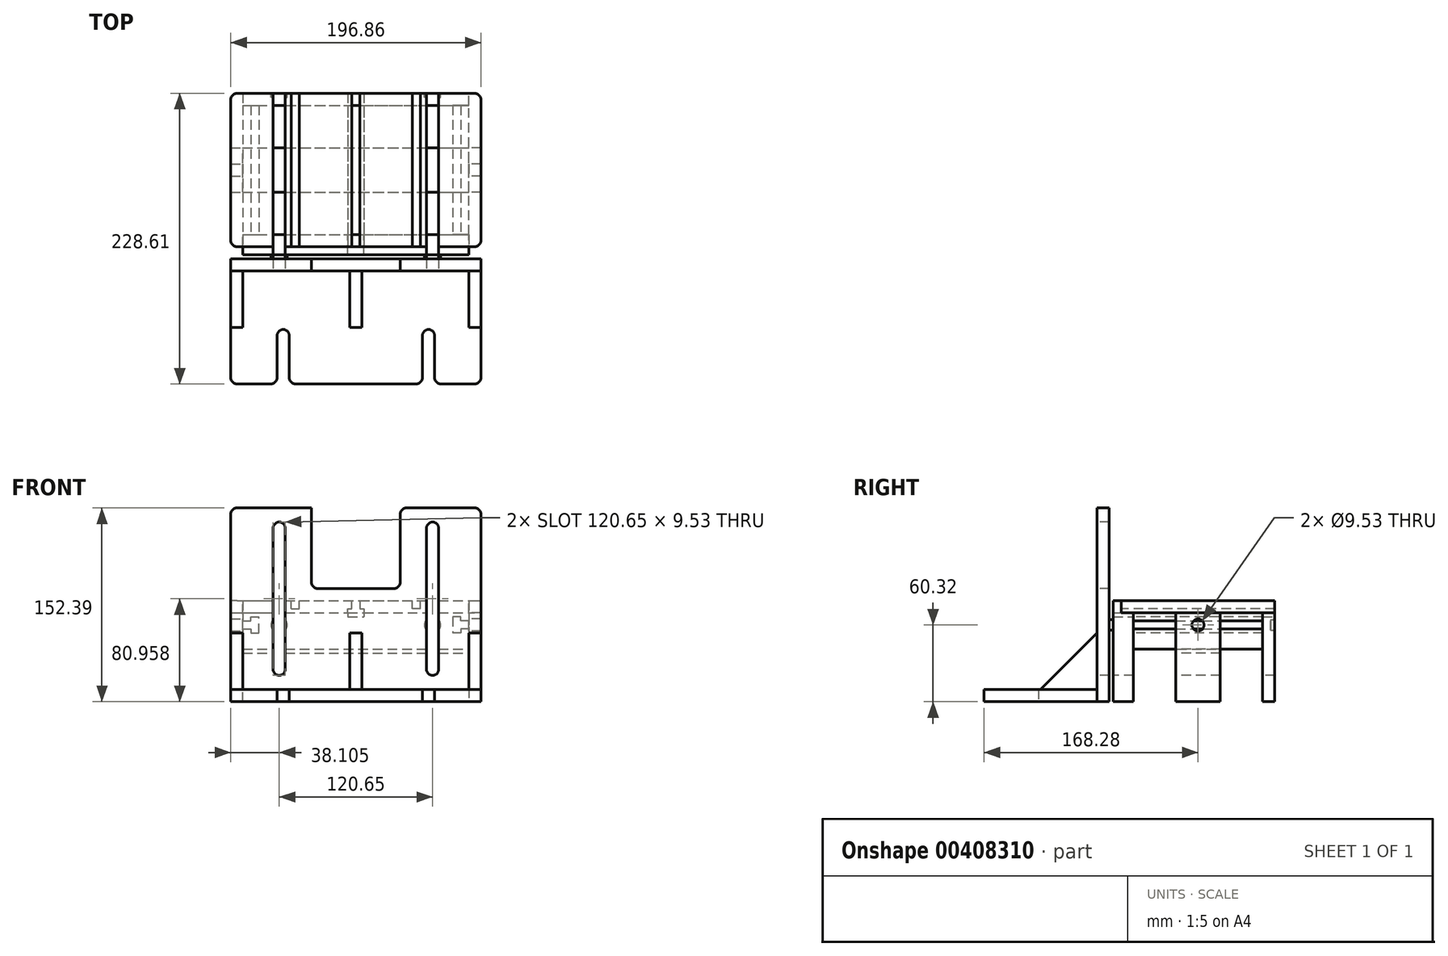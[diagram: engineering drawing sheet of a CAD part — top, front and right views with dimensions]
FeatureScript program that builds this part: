
annotation { "Feature Type Name" : "Feature", "Feature Type Description" : "" }
export const myFeature = defineFeature(function(context is Context, id is Id, definition is map)
    precondition{}
    {
        {
            var Q0;
            Q0=qCreatedBy(makeId("Top.planeOp"),FACE);
            var sketch = newSketch(context, id + "F0", { "sketchPlane" : qUnion([Q0])});
            skLineSegment(sketch, "E0.bottom", {"start": v(-98.42, 60.33) * mm, "end": v(98.43, 60.33) * mm});
            skLineSegment(sketch, "E0.top", {"start": v(-98.43, -60.33) * mm, "end": v(98.42, -60.33) * mm});
            skLineSegment(sketch, "E0.left", {"start": v(-98.42, 60.32) * mm, "end": v(-98.43, -60.33) * mm});
            skLineSegment(sketch, "E0.right", {"start": v(98.43, 60.33) * mm, "end": v(98.42, -60.33) * mm});
            skLineSegment(sketch, "E1", {"start": v(-98.43, 60.33) * mm, "end": v(98.43, -60.33) * mm, "construction": true});
            skSolve(sketch);
        }
        {
            var Q0;
            Q0 = qSketchRegion(id + "F0", true);
            extrude(context, id + "F1", {"entities" : qUnion([Q0]), "depth" : 38.1 * mm});
        }
        {
            var Q0;
            Q0=makeQuery(id+"F1.opExtrude","SWEPT_FACE",FACE,{"disambiguationData":[OSD([sQuery(id+"F0.wireOp",EDGE,"E0.top")])]});
            var sketch = newSketch(context, id + "F2", { "sketchPlane" : qUnion([Q0])});
            skLineSegment(sketch, "E2", {"start": v(-98.43, 19.05) * mm, "end": v(98.43, 19.05) * mm, "construction": true});
            skLineSegment(sketch, "E3", {"start": v(0, 38.1) * mm, "end": v(0, 0) * mm, "construction": true});
            skLineSegment(sketch, "E4", {"start": v(-98.43, 19.05) * mm, "end": v(-98.43, 22.23) * mm});
            skLineSegment(sketch, "E5", {"start": v(-98.42, 22.23) * mm, "end": v(-82.55, 22.23) * mm});
            skLineSegment(sketch, "E6", {"start": v(-82.55, 22.23) * mm, "end": v(-82.55, 25.4) * mm});
            skLineSegment(sketch, "E7", {"start": v(-82.55, 25.4) * mm, "end": v(-76.2, 25.4) * mm});
            skLineSegment(sketch, "E8", {"start": v(-76.2, 25.4) * mm, "end": v(-76.2, 19.05) * mm});
            skLineSegment(sketch, "E9.MirrorCS", {"start": v(-82.55, 15.88) * mm, "end": v(-82.55, 12.7) * mm});
            skLineSegment(sketch, "E10.MirrorCS", {"start": v(-76.2, 12.7) * mm, "end": v(-76.2, 19.05) * mm});
            skLineSegment(sketch, "E11.MirrorCS", {"start": v(-82.55, 12.7) * mm, "end": v(-76.2, 12.7) * mm});
            skLineSegment(sketch, "E12.MirrorCS", {"start": v(-98.42, 15.88) * mm, "end": v(-82.55, 15.88) * mm});
            skLineSegment(sketch, "E13.MirrorCS", {"start": v(-98.43, 19.05) * mm, "end": v(-98.43, 15.88) * mm});
            skLineSegment(sketch, "E14.MirrorCS", {"start": v(82.55, 22.23) * mm, "end": v(82.55, 25.4) * mm});
            skLineSegment(sketch, "E15.MirrorCS", {"start": v(98.42, 19.05) * mm, "end": v(98.42, 15.87) * mm});
            skLineSegment(sketch, "E16.MirrorCS", {"start": v(76.2, 25.4) * mm, "end": v(76.2, 19.05) * mm});
            skLineSegment(sketch, "E17.MirrorCS", {"start": v(82.55, 25.4) * mm, "end": v(76.2, 25.4) * mm});
            skLineSegment(sketch, "E18.MirrorCS", {"start": v(98.42, 22.23) * mm, "end": v(82.55, 22.23) * mm});
            skLineSegment(sketch, "E19.MirrorCS", {"start": v(98.42, 19.05) * mm, "end": v(98.42, 22.23) * mm});
            skLineSegment(sketch, "E20.MirrorCS", {"start": v(82.55, 15.87) * mm, "end": v(82.55, 12.7) * mm});
            skLineSegment(sketch, "E21.MirrorCS", {"start": v(76.2, 12.7) * mm, "end": v(76.2, 19.05) * mm});
            skLineSegment(sketch, "E22.MirrorCS", {"start": v(98.42, 15.88) * mm, "end": v(82.55, 15.88) * mm});
            skLineSegment(sketch, "E23.MirrorCS", {"start": v(82.55, 12.7) * mm, "end": v(76.2, 12.7) * mm});
            skLineSegment(sketch, "E24", {"start": v(-3.18, 38.1) * mm, "end": v(-3.18, 31.75) * mm});
            skLineSegment(sketch, "E25", {"start": v(-3.18, 31.75) * mm, "end": v(-6.35, 31.75) * mm});
            skLineSegment(sketch, "E26", {"start": v(-6.35, 31.75) * mm, "end": v(-6.35, 25.4) * mm});
            skLineSegment(sketch, "E27", {"start": v(-6.35, 25.4) * mm, "end": v(0, 25.4) * mm});
            skLineSegment(sketch, "E28", {"start": v(0, 38.1) * mm, "end": v(-3.18, 38.1) * mm});
            skLineSegment(sketch, "E29.MirrorCS", {"start": v(3.17, 31.75) * mm, "end": v(6.35, 31.75) * mm});
            skLineSegment(sketch, "E30.MirrorCS", {"start": v(0, 38.1) * mm, "end": v(3.17, 38.1) * mm});
            skLineSegment(sketch, "E31.MirrorCS", {"start": v(6.35, 31.75) * mm, "end": v(6.35, 25.4) * mm});
            skLineSegment(sketch, "E32.MirrorCS", {"start": v(6.35, 25.4) * mm, "end": v(0, 25.4) * mm});
            skLineSegment(sketch, "E33.MirrorCS", {"start": v(3.17, 38.1) * mm, "end": v(3.17, 31.75) * mm});
            skSolve(sketch);
        }
        {
            var Q0;
            Q0 = qSketchRegion(id + "F2", true);
            extrude(context, id + "F3", {"entities" : qUnion([Q0]), "operationType" : NewBodyOperationType.REMOVE, "endBound" : BoundingType.THROUGH_ALL, "oppositeDirection" : true, "depth" : 25.4 * mm});
        }
        {
            var Q0;
            Q0=makeQuery(id+"F1.opExtrude","CAP_FACE",FACE,{"disambiguationData":[OSD([sQuery(id+"F0.wireOp",EDGE,"E0.bottom"),sQuery(id+"F0.wireOp",EDGE,"E0.top"),sQuery(id+"F0.wireOp",EDGE,"E0.left"),sQuery(id+"F0.wireOp",EDGE,"E0.right")])],"isStart":true});
            var sketch = newSketch(context, id + "F4", { "sketchPlane" : qUnion([Q0])});
            skLineSegment(sketch, "E34.0", {"start": v(-88.9, 50.8) * mm, "end": v(88.9, 50.8) * mm});
            skLineSegment(sketch, "E34.1", {"start": v(-88.9, -50.8) * mm, "end": v(-88.9, 50.8) * mm});
            skLineSegment(sketch, "E34.2", {"start": v(-88.9, -50.8) * mm, "end": v(88.9, -50.8) * mm});
            skLineSegment(sketch, "E34.3", {"start": v(88.9, -50.8) * mm, "end": v(88.9, 50.8) * mm});
            skSolve(sketch);
        }
        {
            var Q0;
            Q0=makeQuery(id+"F4.imprint","IMPRINT",FACE,{"disambiguationData":[TD([[makeQuery(id+"F4.imprint","IMPRINT",EDGE,{"derivedFrom":sQuery(id+"F4.wireOp",EDGE,"E34.0")}),1.0]])]});
            var Q1;
            Q1=makeQuery(id+"F1.opExtrude","CAP_FACE",FACE,{"disambiguationData":[OSD([sQuery(id+"F0.wireOp",EDGE,"E0.bottom"),sQuery(id+"F0.wireOp",EDGE,"E0.top"),sQuery(id+"F0.wireOp",EDGE,"E0.left"),sQuery(id+"F0.wireOp",EDGE,"E0.right")])],"isStart":false});
            extrude(context, id + "F5", {"entities" : qUnion([Q0]), "operationType" : NewBodyOperationType.REMOVE, "oppositeDirection" : true, "endBoundEntityFace" : qUnion([Q1]), "depth" : 28.57 * mm});
        }
        {
            var Q0;
            {var subQ0=sQuery(id+"F0.wireOp",EDGE,"E0.bottom");var subQ1=sQuery(id+"F0.wireOp",EDGE,"E0.top");var subQ2=sQuery(id+"F0.wireOp",EDGE,"E0.left");Q0=makeQuery(id+"F3.boolean.opBoolean","SPLIT",FACE,{"disambiguationData":[TD([makeQuery(id+"F1.opExtrude","SWEPT_FACE",FACE,{"disambiguationData":[OSD([subQ2])]})])],"derivedFrom":makeQuery(id+"F1.opExtrude","CAP_FACE",FACE,{"disambiguationData":[OSD([subQ0,subQ1,subQ2,sQuery(id+"F0.wireOp",EDGE,"E0.right")])],"isStart":false})});}
            var sketch = newSketch(context, id + "F6", { "sketchPlane" : qUnion([Q0])});
            skLineSegment(sketch, "E35.bottom", {"start": v(-50.8, 60.33) * mm, "end": v(-44.45, 60.33) * mm});
            skLineSegment(sketch, "E35.top", {"start": v(-50.8, -60.33) * mm, "end": v(-44.45, -60.33) * mm});
            skLineSegment(sketch, "E35.left", {"start": v(-50.8, 60.33) * mm, "end": v(-50.8, -60.33) * mm});
            skLineSegment(sketch, "E35.right", {"start": v(-44.45, 60.33) * mm, "end": v(-44.45, -60.33) * mm});
            skLineSegment(sketch, "E36", {"start": v(-47.63, 60.33) * mm, "end": v(-47.62, -60.33) * mm, "construction": true});
            skLineSegment(sketch, "E37", {"start": v(-98.43, 60.33) * mm, "end": v(98.43, -60.33) * mm, "construction": true});
            skLineSegment(sketch, "E38", {"start": v(0, 0) * mm, "end": v(0, 29.12) * mm, "construction": true});
            skLineSegment(sketch, "E39.MirrorCS", {"start": v(50.8, -60.33) * mm, "end": v(44.45, -60.33) * mm});
            skLineSegment(sketch, "E40.MirrorCS", {"start": v(50.8, 60.32) * mm, "end": v(44.45, 60.32) * mm});
            skLineSegment(sketch, "E41.MirrorCS", {"start": v(44.45, 60.33) * mm, "end": v(44.45, -60.33) * mm});
            skLineSegment(sketch, "E42.MirrorCS", {"start": v(50.8, 60.33) * mm, "end": v(50.8, -60.33) * mm});
            skSolve(sketch);
        }
        {
            var Q0;
            Q0 = qSketchRegion(id + "F6", true);
            extrude(context, id + "F7", {"entities" : qUnion([Q0]), "operationType" : NewBodyOperationType.REMOVE, "oppositeDirection" : true, "depth" : 6.35 * mm});
        }
        {
            var Q0;
            {var subQ0=sQuery(id+"F0.wireOp",EDGE,"E0.bottom");var subQ2=sQuery(id+"F0.wireOp",EDGE,"E0.top");var subQ4=sQuery(id+"F0.wireOp",EDGE,"E0.left");var subQ5=makeQuery(id+"F1.opExtrude","SWEPT_FACE",FACE,{"disambiguationData":[OSD([subQ4])]});Q0=makeQuery(id+"F7.boolean.opBoolean","SPLIT",FACE,{"disambiguationData":[TD([subQ5])],"derivedFrom":makeQuery(id+"F3.boolean.opBoolean","SPLIT",FACE,{"disambiguationData":[TD([subQ5])],"derivedFrom":makeQuery(id+"F1.opExtrude","CAP_FACE",FACE,{"disambiguationData":[OSD([subQ0,subQ2,subQ4,sQuery(id+"F0.wireOp",EDGE,"E0.right")])],"isStart":false})})});}
            var sketch = newSketch(context, id + "F8", { "sketchPlane" : qUnion([Q0])});
            skCircle(sketch, "E43", {"center": v(-60.33, 22.23) * mm, "radius": 4.76 * mm});
            skLineSegment(sketch, "E44", {"start": v(-98.43, 0) * mm, "end": v(98.43, 0) * mm, "construction": true});
            skLineSegment(sketch, "E45", {"start": v(0, 0) * mm, "end": v(0, 12.86) * mm, "construction": true});
            skCircle(sketch, "E46.MirrorC", {"center": v(-60.33, -22.23) * mm, "radius": 4.76 * mm});
            skCircle(sketch, "E47.MirrorC", {"center": v(60.33, -22.22) * mm, "radius": 4.76 * mm});
            skCircle(sketch, "E48.MirrorC", {"center": v(60.33, 22.22) * mm, "radius": 4.76 * mm});
            skSolve(sketch);
        }
        {
            var Q0;
            Q0 = qSketchRegion(id + "F8", true);
            extrude(context, id + "F9", {"entities" : qUnion([Q0]), "operationType" : NewBodyOperationType.REMOVE, "oppositeDirection" : true, "depth" : 19.05 * mm});
        }
        {
            var Q0;
            Q0=makeQuery(id+"F5.boolean.opBoolean","COPY",FACE,{"disambiguationData":[TD([makeQuery(id+"F3.boolean.opBoolean","COPY",FACE,{"derivedFrom":makeQuery(id+"F3.opExtrude","SWEPT_FACE",FACE,{"disambiguationData":[OSD([sQuery(id+"F2.wireOp",EDGE,"E22.MirrorCS")])]})})])],"derivedFrom":makeQuery(id+"F5.opExtrude","SWEPT_FACE",FACE,{"disambiguationData":[OSD([sQuery(id+"F4.wireOp",EDGE,"E34.3")])]})});
            var sketch = newSketch(context, id + "F10", { "sketchPlane" : qUnion([Q0])});
            skLineSegment(sketch, "E49", {"start": v(-50.8, 28.58) * mm, "end": v(-60.33, 28.58) * mm});
            skLineSegment(sketch, "E50", {"start": v(-60.33, 28.58) * mm, "end": v(-60.33, 38.1) * mm});
            skLineSegment(sketch, "E51", {"start": v(-60.33, 38.1) * mm, "end": v(-69.85, 38.1) * mm});
            skLineSegment(sketch, "E52", {"start": v(-69.85, 38.1) * mm, "end": v(-69.85, -41.28) * mm});
            skLineSegment(sketch, "E53", {"start": v(-69.85, -41.28) * mm, "end": v(-50.8, -41.28) * mm});
            skLineSegment(sketch, "E54", {"start": v(-50.8, -41.28) * mm, "end": v(-50.8, 28.58) * mm});
            skLineSegment(sketch, "E55.bottom", {"start": v(50.8, 28.58) * mm, "end": v(60.33, 28.58) * mm});
            skLineSegment(sketch, "E55.top", {"start": v(50.8, -41.28) * mm, "end": v(60.33, -41.28) * mm});
            skLineSegment(sketch, "E55.left", {"start": v(50.8, 28.58) * mm, "end": v(50.8, -41.28) * mm});
            skLineSegment(sketch, "E55.right", {"start": v(60.33, 28.58) * mm, "end": v(60.33, -41.28) * mm});
            skSolve(sketch);
        }
        {
            var Q0;
            Q0 = qSketchRegion(id + "F10", true);
            var Q1;
            Q1=makeQuery(id+"F5.boolean.opBoolean","COPY",FACE,{"disambiguationData":[TD([makeQuery(id+"F3.boolean.opBoolean","COPY",FACE,{"derivedFrom":makeQuery(id+"F3.opExtrude","SWEPT_FACE",FACE,{"disambiguationData":[OSD([sQuery(id+"F2.wireOp",EDGE,"E12.MirrorCS")])]})})])],"derivedFrom":makeQuery(id+"F5.opExtrude","SWEPT_FACE",FACE,{"disambiguationData":[OSD([sQuery(id+"F4.wireOp",EDGE,"E34.1")])]})});
            extrude(context, id + "F11", {"entities" : qUnion([Q0]), "endBound" : BoundingType.UP_TO_SURFACE, "oppositeDirection" : true, "endBoundEntityFace" : qUnion([Q1]), "depth" : 25.4 * mm});
        }
        {
            var Q0;
            Q0=makeQuery(id+"F11.opExtrude","SWEPT_FACE",FACE,{"disambiguationData":[OSD([sQuery(id+"F10.wireOp",EDGE,"E55.right")])]});
            var sketch = newSketch(context, id + "F12", { "sketchPlane" : qUnion([Q0])});
            skCircle(sketch, "E56", {"center": v(-60.33, 19.05) * mm, "radius": 4.76 * mm});
            skCircle(sketch, "E57", {"center": v(60.33, 19.05) * mm, "radius": 4.76 * mm});
            skLineSegment(sketch, "E58", {"start": v(-60.33, 19.05) * mm, "end": v(60.33, 19.05) * mm, "construction": true});
            skLineSegment(sketch, "E59", {"start": v(0, 28.58) * mm, "end": v(0, 3.82) * mm, "construction": true});
            skCircle(sketch, "E60", {"center": v(-60.33, 19.05) * mm, "radius": 6.35 * mm});
            skCircle(sketch, "E61", {"center": v(60.33, 19.05) * mm, "radius": 6.35 * mm});
            skLineSegment(sketch, "E62.0", {"start": v(-6.35, 28.57) * mm, "end": v(-6.35, 25.4) * mm});
            skLineSegment(sketch, "E62.1", {"start": v(6.35, 25.4) * mm, "end": v(-6.35, 25.4) * mm});
            skLineSegment(sketch, "E62.2", {"start": v(6.35, 28.57) * mm, "end": v(6.35, 25.4) * mm});
            skLineSegment(sketch, "E63", {"start": v(-6.35, 28.57) * mm, "end": v(6.35, 28.57) * mm});
            skSolve(sketch);
        }
        {
            var Q0;
            Q0=makeQuery(id+"F12.imprint","IMPRINT",FACE,{"disambiguationData":[TD([[makeQuery(id+"F12.imprint","IMPRINT",EDGE,{"derivedFrom":sQuery(id+"F12.wireOp",EDGE,"E56")}),-1.0]])]});
            var Q1;
            Q1=makeQuery(id+"F12.imprint","IMPRINT",FACE,{"disambiguationData":[TD([[makeQuery(id+"F12.imprint","IMPRINT",EDGE,{"derivedFrom":sQuery(id+"F12.wireOp",EDGE,"E56")}),1.0]])]});
            var Q2;
            Q2=makeQuery(id+"F12.imprint","IMPRINT",FACE,{"disambiguationData":[TD([[makeQuery(id+"F12.imprint","IMPRINT",EDGE,{"derivedFrom":sQuery(id+"F12.wireOp",EDGE,"E57")}),-1.0]])]});
            var Q3;
            Q3=makeQuery(id+"F12.imprint","IMPRINT",FACE,{"disambiguationData":[TD([[makeQuery(id+"F12.imprint","IMPRINT",EDGE,{"derivedFrom":sQuery(id+"F12.wireOp",EDGE,"E57")}),1.0]])]});
            var Q4;
            Q4=sQuery(id+"F12.wireOp",EDGE,"E60");
            var Q5;
            Q5=sQuery(id+"F12.wireOp",EDGE,"E61");
            extrude(context, id + "F13", {"entities" : qUnion([Q0, Q1, Q2, Q3]), "operationType" : NewBodyOperationType.REMOVE, "surfaceEntities" : qUnion([Q4, Q5]), "oppositeDirection" : true, "depth" : 3.17 * mm});
        }
        {
            var Q0;
            Q0=makeQuery(id+"F12.imprint","IMPRINT",FACE,{"disambiguationData":[TD([[makeQuery(id+"F12.imprint","IMPRINT",EDGE,{"derivedFrom":sQuery(id+"F12.wireOp",EDGE,"E56")}),1.0]])]});
            var Q1;
            Q1=makeQuery(id+"F12.imprint","IMPRINT",FACE,{"disambiguationData":[TD([[makeQuery(id+"F12.imprint","IMPRINT",EDGE,{"derivedFrom":sQuery(id+"F12.wireOp",EDGE,"E57")}),1.0]])]});
            var Q2;
            Q2=sQuery(id+"F12.wireOp",EDGE,"E56");
            var Q3;
            Q3=sQuery(id+"F12.wireOp",EDGE,"E57");
            extrude(context, id + "F14", {"entities" : qUnion([Q0, Q1]), "operationType" : NewBodyOperationType.REMOVE, "surfaceEntities" : qUnion([Q2, Q3]), "endBound" : BoundingType.THROUGH_ALL, "oppositeDirection" : true, "depth" : 25.4 * mm});
        }
        {
            var Q0;
            Q0=makeQuery(id+"F11.opExtrude","SWEPT_FACE",FACE,{"disambiguationData":[OSD([sQuery(id+"F10.wireOp",EDGE,"E52")])]});
            var sketch = newSketch(context, id + "F15", { "sketchPlane" : qUnion([Q0])});
            skCircle(sketch, "E64.0", {"center": v(-60.33, 19.05) * mm, "radius": 6.35 * mm});
            skCircle(sketch, "E64.1", {"center": v(60.33, 19.05) * mm, "radius": 6.35 * mm});
            skCircle(sketch, "E65", {"center": v(-60.33, -12.7) * mm, "radius": 4.76 * mm});
            skCircle(sketch, "E66", {"center": v(60.33, -12.7) * mm, "radius": 4.76 * mm});
            skSolve(sketch);
        }
        {
            var Q0;
            Q0=makeQuery(id+"F15.imprint","IMPRINT",FACE,{"disambiguationData":[TD([[makeQuery(id+"F15.imprint","IMPRINT",EDGE,{"derivedFrom":makeQuery(id+"F14.boolean.opBoolean","INTERSECT",EDGE,{"derivedFrom":[makeQuery(id+"F11.opExtrude","SWEPT_FACE",FACE,{"disambiguationData":[OSD([sQuery(id+"F10.wireOp",EDGE,"E52")])]}),makeQuery(id+"F14.opExtrude","SWEPT_FACE",FACE,{"disambiguationData":[OSD([sQuery(id+"F12.wireOp",EDGE,"E56")])]})]})}),1.0]])]});
            var Q1;
            Q1=makeQuery(id+"F15.imprint","IMPRINT",FACE,{"disambiguationData":[TD([[makeQuery(id+"F15.imprint","IMPRINT",EDGE,{"derivedFrom":makeQuery(id+"F14.boolean.opBoolean","INTERSECT",EDGE,{"derivedFrom":[makeQuery(id+"F11.opExtrude","SWEPT_FACE",FACE,{"disambiguationData":[OSD([sQuery(id+"F10.wireOp",EDGE,"E52")])]}),makeQuery(id+"F14.opExtrude","SWEPT_FACE",FACE,{"disambiguationData":[OSD([sQuery(id+"F12.wireOp",EDGE,"E57")])]})]})}),1.0]])]});
            var Q2;
            Q2=makeQuery(id+"F15.imprint","IMPRINT",FACE,{"disambiguationData":[TD([[makeQuery(id+"F15.imprint","IMPRINT",EDGE,{"derivedFrom":sQuery(id+"F15.wireOp",EDGE,"E64.0")}),-1.0]])]});
            var Q3;
            Q3=makeQuery(id+"F15.imprint","IMPRINT",FACE,{"disambiguationData":[TD([[makeQuery(id+"F15.imprint","IMPRINT",EDGE,{"derivedFrom":sQuery(id+"F15.wireOp",EDGE,"E64.1")}),-1.0]])]});
            extrude(context, id + "F16", {"entities" : qUnion([Q0, Q1, Q2, Q3]), "operationType" : NewBodyOperationType.REMOVE, "oppositeDirection" : true, "depth" : 3.17 * mm});
        }
        {
            var Q0;
            Q0=makeQuery(id+"F15.imprint","IMPRINT",FACE,{"disambiguationData":[TD([[makeQuery(id+"F15.imprint","IMPRINT",EDGE,{"derivedFrom":sQuery(id+"F15.wireOp",EDGE,"E65")}),1.0]])]});
            var Q1;
            Q1=makeQuery(id+"F15.imprint","IMPRINT",FACE,{"disambiguationData":[TD([[makeQuery(id+"F15.imprint","IMPRINT",EDGE,{"derivedFrom":sQuery(id+"F15.wireOp",EDGE,"E66")}),1.0]])]});
            var Q2;
            Q2=makeQuery(id+"F11.opExtrude","SWEPT_FACE",FACE,{"disambiguationData":[OSD([sQuery(id+"F10.wireOp",EDGE,"E54")])]});
            extrude(context, id + "F17", {"entities" : qUnion([Q0, Q1]), "operationType" : NewBodyOperationType.REMOVE, "endBound" : BoundingType.UP_TO_SURFACE, "oppositeDirection" : true, "endBoundEntityFace" : qUnion([Q2]), "depth" : 25.4 * mm});
        }
        {
            var Q0;
            Q0=makeQuery(id+"F12.imprint","IMPRINT",FACE,{"disambiguationData":[TD([[makeQuery(id+"F12.imprint","IMPRINT",EDGE,{"derivedFrom":sQuery(id+"F12.wireOp",EDGE,"E62.0")}),1.0]])]});
            extrude(context, id + "F18", {"entities" : qUnion([Q0]), "operationType" : NewBodyOperationType.REMOVE, "endBound" : BoundingType.THROUGH_ALL, "oppositeDirection" : true, "depth" : 25.4 * mm});
        }
        {
            var Q0;
            Q0=makeQuery(id+"F5.boolean.opBoolean","COPY",FACE,{"disambiguationData":[TD([makeQuery(id+"F3.boolean.opBoolean","COPY",FACE,{"derivedFrom":makeQuery(id+"F3.opExtrude","SWEPT_FACE",FACE,{"disambiguationData":[OSD([sQuery(id+"F2.wireOp",EDGE,"E22.MirrorCS")])]})})])],"derivedFrom":makeQuery(id+"F5.opExtrude","SWEPT_FACE",FACE,{"disambiguationData":[OSD([sQuery(id+"F4.wireOp",EDGE,"E34.3")])]})});
            var sketch = newSketch(context, id + "F19", { "sketchPlane" : qUnion([Q0])});
            skLineSegment(sketch, "E67.top", {"start": v(-17.46, -41.28) * mm, "end": v(17.46, -41.28) * mm});
            skLineSegment(sketch, "E67.left", {"start": v(-17.46, -3.18) * mm, "end": v(-17.46, -41.28) * mm});
            skLineSegment(sketch, "E67.right", {"start": v(17.46, -3.17) * mm, "end": v(17.46, -41.27) * mm});
            skLineSegment(sketch, "E68", {"start": v(0, 15.88) * mm, "end": v(0, -3.18) * mm, "construction": true});
            skLineSegment(sketch, "E69", {"start": v(-17.46, -3.18) * mm, "end": v(17.46, -3.18) * mm});
            skSolve(sketch);
        }
        {
            var Q0;
            Q0 = qSketchRegion(id + "F19", true);
            var Q1;
            Q1=makeQuery(id+"F5.boolean.opBoolean","COPY",FACE,{"disambiguationData":[TD([makeQuery(id+"F3.boolean.opBoolean","COPY",FACE,{"derivedFrom":makeQuery(id+"F3.opExtrude","SWEPT_FACE",FACE,{"disambiguationData":[OSD([sQuery(id+"F2.wireOp",EDGE,"E12.MirrorCS")])]})})])],"derivedFrom":makeQuery(id+"F5.opExtrude","SWEPT_FACE",FACE,{"disambiguationData":[OSD([sQuery(id+"F4.wireOp",EDGE,"E34.1")])]})});
            extrude(context, id + "F20", {"entities" : qUnion([Q0]), "endBound" : BoundingType.UP_TO_SURFACE, "oppositeDirection" : true, "endBoundEntityFace" : qUnion([Q1]), "depth" : 25.4 * mm});
        }
        {
            var Q0;
            Q0=makeQuery(id+"F20.opExtrude","CAP_FACE",FACE,{"disambiguationData":[OSD([sQuery(id+"F19.wireOp",EDGE,"E67.bottom"),sQuery(id+"F19.wireOp",EDGE,"E67.top"),sQuery(id+"F19.wireOp",EDGE,"E67.left"),sQuery(id+"F19.wireOp",EDGE,"E67.right")])],"isStart":true});
            var sketch = newSketch(context, id + "F21", { "sketchPlane" : qUnion([Q0])});
            skLineSegment(sketch, "E70.bottom", {"start": v(-17.46, -41.28) * mm, "end": v(17.46, -41.28) * mm});
            skLineSegment(sketch, "E70.top", {"start": v(-17.46, 28.58) * mm, "end": v(17.46, 28.58) * mm});
            skLineSegment(sketch, "E70.left", {"start": v(-17.46, -41.28) * mm, "end": v(-17.46, 28.58) * mm});
            skLineSegment(sketch, "E70.right", {"start": v(17.46, -41.28) * mm, "end": v(17.46, 28.58) * mm});
            skLineSegment(sketch, "E71", {"start": v(-17.46, 15.88) * mm, "end": v(17.46, 22.23) * mm, "construction": true});
            skCircle(sketch, "E72", {"center": v(0, 19.05) * mm, "radius": 4.76 * mm});
            skSolve(sketch);
        }
        {
            var Q0;
            Q0 = qSketchRegion(id + "F21", true);
            extrude(context, id + "F22", {"entities" : qUnion([Q0]), "depth" : 9.52 * mm});
        }
        {
            var Q0;
            Q0=makeQuery(id+"F22.opExtrude","SWEPT_BODY",BODY,{"disambiguationData":[OSD([sQuery(id+"F21.wireOp",EDGE,"E70.bottom"),sQuery(id+"F21.wireOp",EDGE,"E70.top"),sQuery(id+"F21.wireOp",EDGE,"E70.left"),sQuery(id+"F21.wireOp",EDGE,"E70.right"),sQuery(id+"F21.wireOp",EDGE,"E72")])]});
            var Q1;
            Q1=qCreatedBy(makeId("Right.planeOp"),FACE);
            mirror(context, id + "F23", {"entities" : qUnion([Q0]), "mirrorPlane" : qUnion([Q1])});
        }
        {
            var Q0;
            Q0=makeQuery(id+"F11.opExtrude","SWEPT_FACE",FACE,{"disambiguationData":[OSD([sQuery(id+"F10.wireOp",EDGE,"E52")])]});
            var sketch = newSketch(context, id + "F24", { "sketchPlane" : qUnion([Q0])});
            skLineSegment(sketch, "E73.bottom", {"start": v(-98.43, 111.13) * mm, "end": v(98.43, 111.13) * mm});
            skLineSegment(sketch, "E73.top", {"start": v(-98.43, -41.27) * mm, "end": v(98.43, -41.27) * mm});
            skLineSegment(sketch, "E73.left", {"start": v(-98.43, 111.13) * mm, "end": v(-98.43, -41.27) * mm});
            skLineSegment(sketch, "E73.right", {"start": v(98.43, 111.13) * mm, "end": v(98.43, -41.27) * mm});
            skSolve(sketch);
        }
        {
            var Q0;
            Q0 = qSketchRegion(id + "F24", true);
            extrude(context, id + "F25", {"entities" : qUnion([Q0]), "depth" : 9.52 * mm});
        }
        {
            var Q0;
            Q0=makeQuery(id+"F25.opExtrude","CAP_FACE",FACE,{"disambiguationData":[OSD([sQuery(id+"F24.wireOp",EDGE,"E73.bottom"),sQuery(id+"F24.wireOp",EDGE,"E73.top"),sQuery(id+"F24.wireOp",EDGE,"E73.left"),sQuery(id+"F24.wireOp",EDGE,"E73.right")])],"isStart":false});
            var sketch = newSketch(context, id + "F26", { "sketchPlane" : qUnion([Q0])});
            skLineSegment(sketch, "E74.left", {"start": v(-55.56, -15.88) * mm, "end": v(-55.56, 95.25) * mm});
            skLineSegment(sketch, "E74.right", {"start": v(-65.09, -15.88) * mm, "end": v(-65.09, 95.25) * mm});
            skPoint(sketch, "E74.middle", {"position": v(-60.33, 39.69) * mm});
            skArc(sketch, "E75", {"start": v(-55.56, 95.25) * mm, "mid": v(-60.33, 100.01) * mm, "end": v(-65.09, 95.25) * mm});
            skArc(sketch, "E76", {"start": v(-65.09, -15.87) * mm, "mid": v(-60.33, -20.64) * mm, "end": v(-55.56, -15.87) * mm});
            skLineSegment(sketch, "E77", {"start": v(0, 111.13) * mm, "end": v(0, -41.28) * mm, "construction": true});
            skLineSegment(sketch, "E78.MirrorCS", {"start": v(55.56, -15.87) * mm, "end": v(55.56, 95.25) * mm});
            skLineSegment(sketch, "E79.MirrorCS", {"start": v(65.09, -15.87) * mm, "end": v(65.09, 95.25) * mm});
            skArc(sketch, "E80.MirrorCS", {"start": v(55.56, 95.25) * mm, "mid": v(60.33, 100.01) * mm, "end": v(65.09, 95.25) * mm});
            skPoint(sketch, "E81.MirrorP", {"position": v(60.33, 39.69) * mm});
            skArc(sketch, "E82.MirrorCS", {"start": v(65.09, -15.87) * mm, "mid": v(60.33, -20.64) * mm, "end": v(55.56, -15.87) * mm});
            skLineSegment(sketch, "E83.bottom", {"start": v(-34.93, 111.13) * mm, "end": v(34.93, 111.13) * mm});
            skLineSegment(sketch, "E83.top", {"start": v(-34.93, 47.63) * mm, "end": v(34.93, 47.63) * mm});
            skLineSegment(sketch, "E83.left", {"start": v(-34.93, 111.13) * mm, "end": v(-34.93, 47.63) * mm});
            skLineSegment(sketch, "E83.right", {"start": v(34.93, 111.13) * mm, "end": v(34.93, 47.63) * mm});
            skSolve(sketch);
        }
        {
            var Q0;
            Q0 = qSketchRegion(id + "F26", true);
            extrude(context, id + "F27", {"entities" : qUnion([Q0]), "operationType" : NewBodyOperationType.REMOVE, "endBound" : BoundingType.THROUGH_ALL, "oppositeDirection" : true, "depth" : 25.4 * mm});
        }
        {
            var Q0;
            Q0=makeQuery(id+"F25.opExtrude","CAP_FACE",FACE,{"disambiguationData":[OSD([sQuery(id+"F24.wireOp",EDGE,"E73.bottom"),sQuery(id+"F24.wireOp",EDGE,"E73.top"),sQuery(id+"F24.wireOp",EDGE,"E73.left"),sQuery(id+"F24.wireOp",EDGE,"E73.right")])],"isStart":false});
            var sketch = newSketch(context, id + "F28", { "sketchPlane" : qUnion([Q0])});
            skLineSegment(sketch, "E84.bottom", {"start": v(-98.43, -31.75) * mm, "end": v(-88.9, -31.75) * mm});
            skLineSegment(sketch, "E84.top", {"start": v(-98.43, 12.7) * mm, "end": v(-88.9, 12.7) * mm});
            skLineSegment(sketch, "E84.left", {"start": v(-98.43, -31.75) * mm, "end": v(-98.43, 12.7) * mm});
            skLineSegment(sketch, "E84.right", {"start": v(-88.9, -31.75) * mm, "end": v(-88.9, 12.7) * mm});
            skLineSegment(sketch, "E85.bottom", {"start": v(98.43, -31.75) * mm, "end": v(88.9, -31.75) * mm});
            skLineSegment(sketch, "E85.top", {"start": v(98.43, 12.7) * mm, "end": v(88.9, 12.7) * mm});
            skLineSegment(sketch, "E85.left", {"start": v(98.43, -31.75) * mm, "end": v(98.43, 12.7) * mm});
            skLineSegment(sketch, "E85.right", {"start": v(88.9, -31.75) * mm, "end": v(88.9, 12.7) * mm});
            skLineSegment(sketch, "E86.top", {"start": v(-4.76, 12.7) * mm, "end": v(4.76, 12.7) * mm});
            skLineSegment(sketch, "E86.left", {"start": v(4.76, -31.75) * mm, "end": v(4.76, 12.7) * mm});
            skLineSegment(sketch, "E86.right", {"start": v(-4.76, -31.75) * mm, "end": v(-4.76, 12.7) * mm});
            skLineSegment(sketch, "E87", {"start": v(0, -41.27) * mm, "end": v(0, 12.7) * mm, "construction": true});
            skLineSegment(sketch, "E88", {"start": v(-4.76, -31.75) * mm, "end": v(4.76, -31.75) * mm});
            skSolve(sketch);
        }
        {
            var Q0;
            Q0 = qSketchRegion(id + "F28", true);
            extrude(context, id + "F29", {"entities" : qUnion([Q0]), "depth" : 44.45 * mm});
        }
        {
            var Q0;
            Q0=makeQuery(id+"F29.opExtrude","SWEPT_FACE",FACE,{"disambiguationData":[OSD([sQuery(id+"F28.wireOp",EDGE,"E84.left")])]});
            var sketch = newSketch(context, id + "F30", { "sketchPlane" : qUnion([Q0])});
            skLineSegment(sketch, "E89", {"start": v(79.38, 12.7) * mm, "end": v(123.83, -31.75) * mm});
            skLineSegment(sketch, "E90", {"start": v(123.83, -31.75) * mm, "end": v(123.83, 12.7) * mm});
            skLineSegment(sketch, "E91", {"start": v(123.83, 12.7) * mm, "end": v(79.38, 12.7) * mm});
            skSolve(sketch);
        }
        {
            var Q0;
            Q0 = qSketchRegion(id + "F30", true);
            extrude(context, id + "F31", {"entities" : qUnion([Q0]), "operationType" : NewBodyOperationType.REMOVE, "endBound" : BoundingType.THROUGH_ALL, "oppositeDirection" : true, "depth" : 25.4 * mm});
        }
        {
            var Q0;
            Q0=makeQuery(id+"F25.opExtrude","SWEPT_FACE",FACE,{"disambiguationData":[OSD([sQuery(id+"F24.wireOp",EDGE,"E73.top")])]});
            var sketch = newSketch(context, id + "F32", { "sketchPlane" : qUnion([Q0])});
            skLineSegment(sketch, "E92.bottom", {"start": v(-98.43, 79.38) * mm, "end": v(98.42, 79.38) * mm});
            skLineSegment(sketch, "E92.top", {"start": v(-98.43, 168.28) * mm, "end": v(-61.91, 168.28) * mm});
            skLineSegment(sketch, "E92.left", {"start": v(-98.43, 79.38) * mm, "end": v(-98.43, 168.28) * mm});
            skLineSegment(sketch, "E92.right", {"start": v(98.42, 79.38) * mm, "end": v(98.42, 168.28) * mm});
            skLineSegment(sketch, "E93", {"start": v(0, 168.28) * mm, "end": v(0, 131.76) * mm, "construction": true});
            skLineSegment(sketch, "E94.left", {"start": v(-52.39, 130.18) * mm, "end": v(-52.39, 168.28) * mm});
            skLineSegment(sketch, "E94.right", {"start": v(-61.91, 130.18) * mm, "end": v(-61.91, 168.28) * mm});
            skPoint(sketch, "E94.middle", {"position": v(-57.15, 149.23) * mm});
            skArc(sketch, "E95", {"start": v(-61.91, 130.18) * mm, "mid": v(-57.15, 125.41) * mm, "end": v(-52.39, 130.18) * mm});
            skLineSegment(sketch, "E96.trimOffspring", {"start": v(-52.39, 168.28) * mm, "end": v(52.39, 168.28) * mm});
            skArc(sketch, "E97.MirrorCS", {"start": v(61.91, 130.18) * mm, "mid": v(57.15, 125.41) * mm, "end": v(52.39, 130.18) * mm});
            skPoint(sketch, "E98.MirrorP", {"position": v(57.15, 149.23) * mm});
            skLineSegment(sketch, "E99.MirrorCS", {"start": v(52.39, 130.18) * mm, "end": v(52.39, 168.28) * mm});
            skLineSegment(sketch, "E100.MirrorCS", {"start": v(61.91, 130.18) * mm, "end": v(61.91, 168.28) * mm});
            skLineSegment(sketch, "E101.trimOffspring", {"start": v(61.91, 168.28) * mm, "end": v(98.42, 168.28) * mm});
            skSolve(sketch);
        }
        {
            var Q0;
            Q0 = qSketchRegion(id + "F32", true);
            extrude(context, id + "F33", {"entities" : qUnion([Q0]), "oppositeDirection" : true, "depth" : 9.52 * mm});
        }
        {
            var Q0;
            Q0=makeQuery(id+"F25.opExtrude","SWEPT_EDGE",EDGE,{"disambiguationData":[OSD([sQuery(id+"F24.wireOp",EDGE,"E73.bottom"),sQuery(id+"F24.wireOp",EDGE,"E73.left")])]});
            var Q1;
            Q1=makeQuery(id+"F27.boolean.opBoolean","COPY",EDGE,{"derivedFrom":makeQuery(id+"F27.opExtrude","SWEPT_EDGE",EDGE,{"disambiguationData":[OSD([sQuery(id+"F24.wireOp",EDGE,"E73.bottom"),sQuery(id+"F26.wireOp",EDGE,"E83.bottom"),sQuery(id+"F26.wireOp",EDGE,"E83.left")])]})});
            var Q2;
            Q2=makeQuery(id+"F27.boolean.opBoolean","COPY",EDGE,{"derivedFrom":makeQuery(id+"F27.opExtrude","SWEPT_EDGE",EDGE,{"disambiguationData":[OSD([sQuery(id+"F24.wireOp",EDGE,"E73.bottom"),sQuery(id+"F26.wireOp",EDGE,"E83.bottom"),sQuery(id+"F26.wireOp",EDGE,"E83.right")])]})});
            var Q3;
            Q3=makeQuery(id+"F25.opExtrude","SWEPT_EDGE",EDGE,{"disambiguationData":[OSD([sQuery(id+"F24.wireOp",EDGE,"E73.bottom"),sQuery(id+"F24.wireOp",EDGE,"E73.right")])]});
            var Q4;
            Q4=makeQuery(id+"F27.boolean.opBoolean","COPY",EDGE,{"derivedFrom":makeQuery(id+"F27.opExtrude","SWEPT_EDGE",EDGE,{"disambiguationData":[OSD([sQuery(id+"F26.wireOp",EDGE,"E83.top"),sQuery(id+"F26.wireOp",EDGE,"E83.left")])]})});
            var Q5;
            Q5=makeQuery(id+"F27.boolean.opBoolean","COPY",EDGE,{"derivedFrom":makeQuery(id+"F27.opExtrude","SWEPT_EDGE",EDGE,{"disambiguationData":[OSD([sQuery(id+"F26.wireOp",EDGE,"E83.top"),sQuery(id+"F26.wireOp",EDGE,"E83.right")])]})});
            var Q6;
            Q6=makeQuery(id+"F33.opExtrude","SWEPT_EDGE",EDGE,{"disambiguationData":[OSD([sQuery(id+"F32.wireOp",EDGE,"E92.top"),sQuery(id+"F32.wireOp",EDGE,"E94.right")])]});
            var Q7;
            Q7=makeQuery(id+"F33.opExtrude","SWEPT_EDGE",EDGE,{"disambiguationData":[OSD([sQuery(id+"F32.wireOp",EDGE,"E94.left"),sQuery(id+"F32.wireOp",EDGE,"E96.trimOffspring")])]});
            var Q8;
            Q8=makeQuery(id+"F33.opExtrude","SWEPT_EDGE",EDGE,{"disambiguationData":[OSD([sQuery(id+"F32.wireOp",EDGE,"E96.trimOffspring"),sQuery(id+"F32.wireOp",EDGE,"E99.MirrorCS")])]});
            var Q9;
            Q9=makeQuery(id+"F33.opExtrude","SWEPT_EDGE",EDGE,{"disambiguationData":[OSD([sQuery(id+"F32.wireOp",EDGE,"E100.MirrorCS"),sQuery(id+"F32.wireOp",EDGE,"E101.trimOffspring")])]});
            var Q10;
            Q10=makeQuery(id+"F33.opExtrude","SWEPT_EDGE",EDGE,{"disambiguationData":[OSD([sQuery(id+"F32.wireOp",EDGE,"E92.top"),sQuery(id+"F32.wireOp",EDGE,"E92.left")])]});
            var Q11;
            Q11=makeQuery(id+"F33.opExtrude","SWEPT_EDGE",EDGE,{"disambiguationData":[OSD([sQuery(id+"F32.wireOp",EDGE,"E92.right"),sQuery(id+"F32.wireOp",EDGE,"E101.trimOffspring")])]});
            var Q12;
            {var subQ0=sQuery(id+"F0.wireOp",EDGE,"E0.bottom");var subQ1=sQuery(id+"F0.wireOp",EDGE,"E0.right");Q12=makeQuery(id+"F3.boolean.opBoolean","SPLIT",EDGE,{"disambiguationData":[TD([makeQuery(id+"F3.opExtrude","SWEPT_FACE",FACE,{"disambiguationData":[OSD([sQuery(id+"F2.wireOp",EDGE,"E18.MirrorCS")])]})])],"derivedFrom":makeQuery(id+"F1.opExtrude","SWEPT_EDGE",EDGE,{"disambiguationData":[OSD([subQ0,subQ1])]})});}
            var Q13;
            {var subQ0=sQuery(id+"F0.wireOp",EDGE,"E0.right");var subQ1=sQuery(id+"F0.wireOp",EDGE,"E0.top");Q13=makeQuery(id+"F3.boolean.opBoolean","SPLIT",EDGE,{"disambiguationData":[TD([makeQuery(id+"F3.opExtrude","SWEPT_FACE",FACE,{"disambiguationData":[OSD([sQuery(id+"F2.wireOp",EDGE,"E18.MirrorCS")])]})])],"derivedFrom":makeQuery(id+"F1.opExtrude","SWEPT_EDGE",EDGE,{"disambiguationData":[OSD([subQ1,subQ0])]})});}
            var Q14;
            {var subQ0=sQuery(id+"F0.wireOp",EDGE,"E0.left");var subQ1=sQuery(id+"F0.wireOp",EDGE,"E0.top");Q14=makeQuery(id+"F3.boolean.opBoolean","SPLIT",EDGE,{"disambiguationData":[TD([makeQuery(id+"F3.opExtrude","SWEPT_FACE",FACE,{"disambiguationData":[OSD([sQuery(id+"F2.wireOp",EDGE,"E5")])]})])],"derivedFrom":makeQuery(id+"F1.opExtrude","SWEPT_EDGE",EDGE,{"disambiguationData":[OSD([subQ1,subQ0])]})});}
            var Q15;
            {var subQ0=sQuery(id+"F0.wireOp",EDGE,"E0.bottom");var subQ1=sQuery(id+"F0.wireOp",EDGE,"E0.left");Q15=makeQuery(id+"F3.boolean.opBoolean","SPLIT",EDGE,{"disambiguationData":[TD([makeQuery(id+"F3.opExtrude","SWEPT_FACE",FACE,{"disambiguationData":[OSD([sQuery(id+"F2.wireOp",EDGE,"E5")])]})])],"derivedFrom":makeQuery(id+"F1.opExtrude","SWEPT_EDGE",EDGE,{"disambiguationData":[OSD([subQ0,subQ1])]})});}
            fillet(context, id + "F34", {"entities" : qUnion([Q0, Q1, Q2, Q3, Q4, Q5, Q6, Q7, Q8, Q9, Q10, Q11, Q12, Q13, Q14, Q15]), "radius" : 5.08 * mm, "tangentPropagation" : true, "allowEdgeOverflow" : false});
        }
    });
